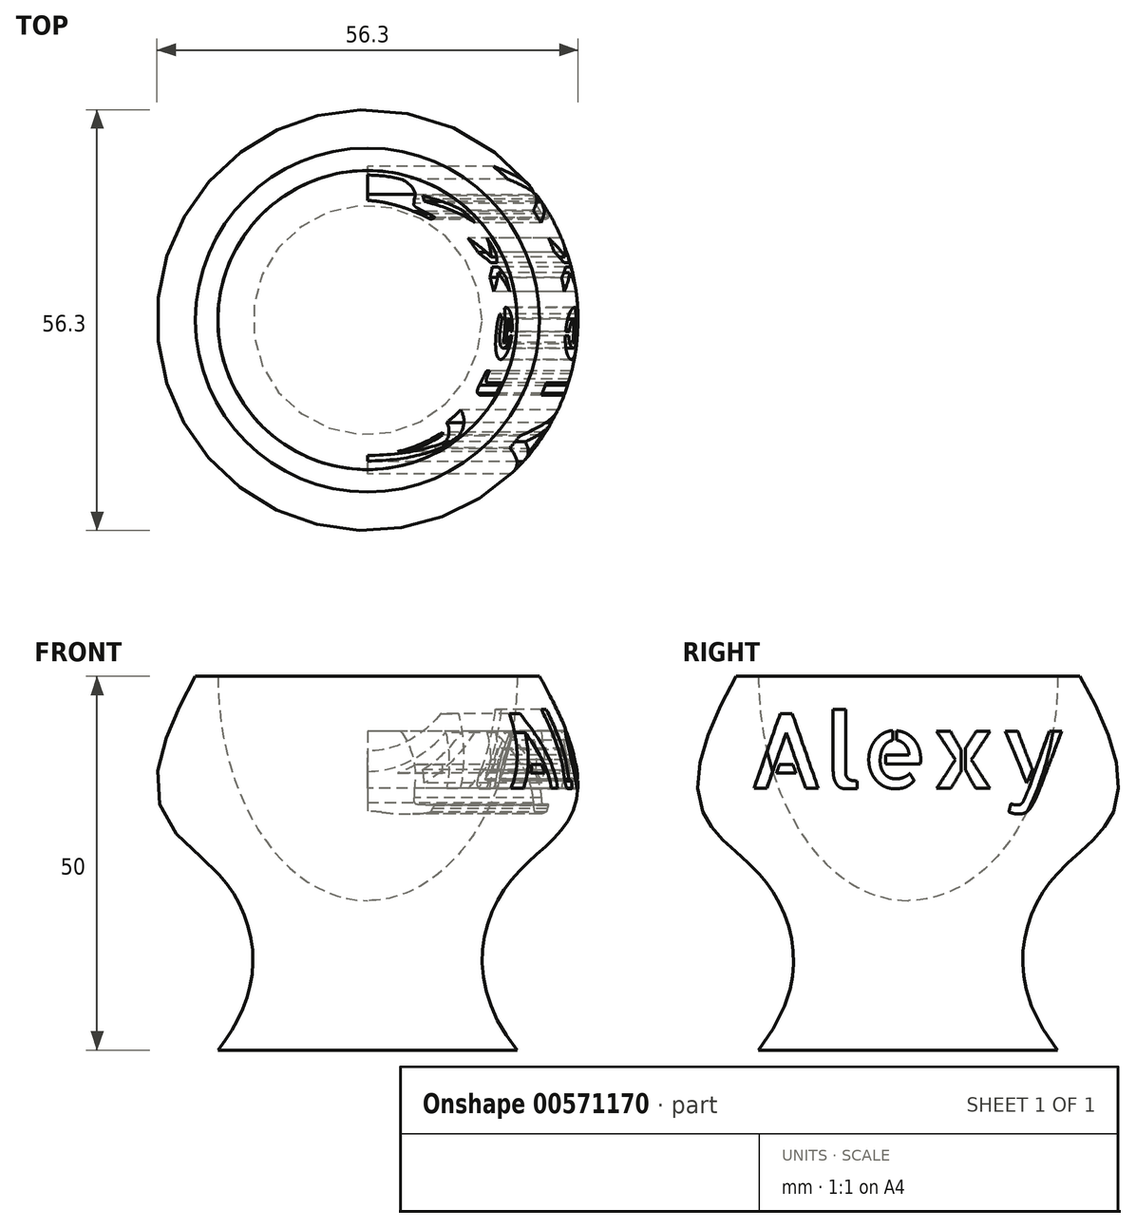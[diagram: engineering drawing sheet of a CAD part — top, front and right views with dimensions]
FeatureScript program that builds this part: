
annotation { "Feature Type Name" : "Feature", "Feature Type Description" : "" }
export const myFeature = defineFeature(function(context is Context, id is Id, definition is map)
    precondition{}
    {
        {
            var Q0;
            Q0=qCreatedBy(makeId("Front.planeOp"),FACE);
            var sketch = newSketch(context, id + "F0", { "sketchPlane" : qUnion([Q0])});
            skEllipse(sketch, "E0", {"center": v(0, 0) * mm, "majorRadius": 30 * mm, "minorRadius": 20 * mm, "majorAxis": v(0, 1)});
            skLineSegment(sketch, "E1", {"start": v(0, 53.08) * mm, "end": v(0, -50) * mm, "construction": true});
            skPoint(sketch, "E1.endSnap0", {"position": v(0, 30) * mm});
            skLineSegment(sketch, "E2", {"start": v(-20, 0) * mm, "end": v(-23, 0) * mm});
            skLineSegment(sketch, "E3", {"start": v(0, -50) * mm, "end": v(-20, -50) * mm});
            skFitSpline(sketch, "E4", {"points": [v(-23, 0) * mm, v(-20, -26.34) * mm, v(-20, -50) * mm], "startDerivative": vector(-62.2, -109.55) * mm, "endDerivative": vector(-45.32, -56.23) * mm});
            skLineSegment(sketch, "E5", {"start": v(0, -50) * mm, "end": v(0, -30) * mm});
            skSolve(sketch);
        }
        {
            var Q0;
            {var subQ0=sQuery(id+"F0.wireOp",EDGE,"E2");Q0=makeQuery(id+"F0.imprint","IMPRINT",FACE,{"disambiguationData":[TD([[makeQuery(id+"F0.imprint","IMPRINT",EDGE,{"derivedFrom":subQ0}),1.0]])]});}
            var Q1;
            Q1=sQuery(id+"F0.wireOp",EDGE,"E1");
            revolve(context, id + "F1", {"entities" : qUnion([Q0]), "axis" : qUnion([Q1]), "revolveType" : RevolveType.FULL});
        }
        {
            var Q0;
            Q0=qCreatedBy(makeId("Right.planeOp"),FACE);
            var sketch = newSketch(context, id + "F2", { "sketchPlane" : qUnion([Q0])});
            skText(sketch, "E6", { "text": "Alexy", "fontName": "AllertaStencil-Regular.ttf"});
            const initialGuessF2  = {"E6": [-0.02146, -0.015, 1, 0, 0.01]};
            skSetInitialGuess(sketch, initialGuessF2);
            skSolve(sketch);
        }
        {
            var Q0;
            Q0 = qSketchRegion(id + "F2", true);
            extrude(context, id + "F3", {"entities" : qUnion([Q0]), "operationType" : NewBodyOperationType.REMOVE, "depth" : 79 * mm, "offsetDistance" : 25 * mm});
        }
    });
